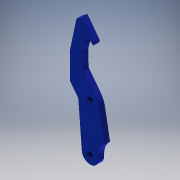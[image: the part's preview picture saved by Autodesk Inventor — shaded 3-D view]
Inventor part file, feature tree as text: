
AUTODESK INVENTOR PART (.ipt)
format: ipt  version: 2016 (Build 200138000, 138)  size: 163,840 bytes
history: native  units: in
note: dims shown in document units (in); Inventor stores cm internally (conversion verified against a paired STEP export)
features: fillet x3, extrude x1, sketch x1
ambient origin geometry x8: Origin, YZ Plane, XZ Plane, XY Plane, X Axis, Y Axis, Z Axis, Center Point
bodies: Solid1 (feature_tree)
feature tree (5):
  extrude  "Extrusion1"  Depth=0.1181in
  fillet  "Fillet1"  Radius=1.0236in
  fillet  "Fillet6"  Radius=0.3543in
  fillet  "Fillet7"  Radius=0.3142in
  sketch  "Sketch1"  dims[d0=0.1181in d1=0.1181in d2=1.0236in d3=0.3543in d4=0.3142in d6=0.65in d14=0.1181in d15=0.0in d16=0.3937in d20=0.5906in d34=0.4331in d35=0.0512in]
